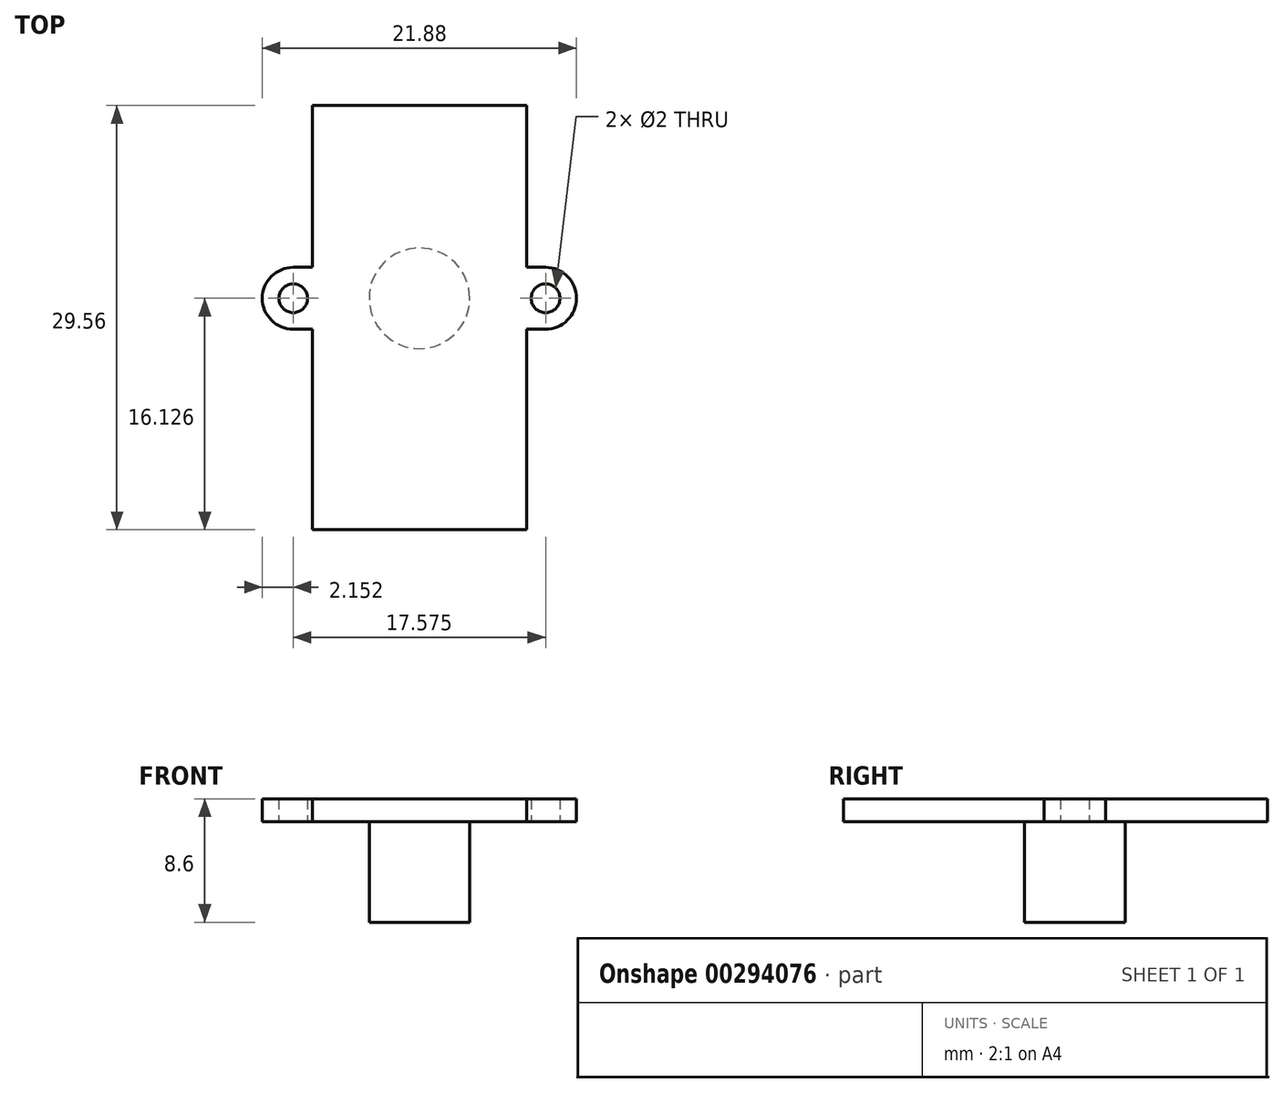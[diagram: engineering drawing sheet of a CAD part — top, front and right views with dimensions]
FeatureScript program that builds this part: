
annotation { "Feature Type Name" : "Feature", "Feature Type Description" : "" }
export const myFeature = defineFeature(function(context is Context, id is Id, definition is map)
    precondition{}
    {
        {
            var Q0;
            Q0=qCreatedBy(makeId("Top.planeOp"),FACE);
            var sketch = newSketch(context, id + "F0", { "sketchPlane" : qUnion([Q0])});
            skLineSegment(sketch, "E0.bottom", {"start": v(-23.3, 24.89) * mm, "end": v(-8.37, 24.89) * mm});
            skLineSegment(sketch, "E0.top", {"start": v(-23.3, -4.67) * mm, "end": v(-8.37, -4.67) * mm});
            skLineSegment(sketch, "E0.left", {"start": v(-23.3, 24.89) * mm, "end": v(-23.3, 13.61) * mm});
            skLineSegment(sketch, "E0.right", {"start": v(-8.37, 24.89) * mm, "end": v(-8.37, 13.61) * mm});
            skLineSegment(sketch, "E1", {"start": v(-23.3, 13.61) * mm, "end": v(-24.63, 13.61) * mm});
            skLineSegment(sketch, "E2", {"start": v(-23.3, 9.3) * mm, "end": v(-24.63, 9.3) * mm});
            skArc(sketch, "E3", {"start": v(-24.63, 13.61) * mm, "mid": v(-26.78, 11.46) * mm, "end": v(-24.63, 9.3) * mm});
            skLineSegment(sketch, "E4", {"start": v(-8.37, 13.61) * mm, "end": v(-7.05, 13.61) * mm});
            skLineSegment(sketch, "E5", {"start": v(-8.37, 9.3) * mm, "end": v(-7.05, 9.3) * mm});
            skArc(sketch, "E6", {"start": v(-7.05, 9.3) * mm, "mid": v(-4.9, 11.46) * mm, "end": v(-7.05, 13.61) * mm});
            skCircle(sketch, "E7", {"center": v(-24.63, 11.46) * mm, "radius": 1 * mm});
            skCircle(sketch, "E8", {"center": v(-7.05, 11.46) * mm, "radius": 1 * mm});
            skLineSegment(sketch, "E9.trimOffspring", {"start": v(-23.3, 9.3) * mm, "end": v(-23.3, -4.67) * mm});
            skLineSegment(sketch, "E10.trimOffspring", {"start": v(-8.37, 9.3) * mm, "end": v(-8.37, -4.67) * mm});
            skLineSegment(sketch, "E11", {"start": v(-24.63, 11.46) * mm, "end": v(-7.05, 11.46) * mm, "construction": true});
            skCircle(sketch, "E12", {"center": v(-15.84, 11.46) * mm, "radius": 3.5 * mm});
            skSolve(sketch);
        }
        {
            var Q0;
            Q0=makeQuery(id+"F0.imprint","IMPRINT",FACE,{"disambiguationData":[TD([[makeQuery(id+"F0.imprint","IMPRINT",EDGE,{"derivedFrom":sQuery(id+"F0.wireOp",EDGE,"E0.bottom")}),-1.0]])]});
            var Q1;
            Q1=makeQuery(id+"F0.imprint","IMPRINT",FACE,{"disambiguationData":[TD([[makeQuery(id+"F0.imprint","IMPRINT",EDGE,{"derivedFrom":sQuery(id+"F0.wireOp",EDGE,"E12")}),1.0]])]});
            extrude(context, id + "F1", {"entities" : qUnion([Q0, Q1]), "depth" : 1.6 * mm});
        }
        {
            var Q0;
            Q0=makeQuery(id+"F0.imprint","IMPRINT",FACE,{"disambiguationData":[TD([[makeQuery(id+"F0.imprint","IMPRINT",EDGE,{"derivedFrom":sQuery(id+"F0.wireOp",EDGE,"E12")}),1.0]])]});
            extrude(context, id + "F2", {"entities" : qUnion([Q0]), "operationType" : NewBodyOperationType.ADD, "oppositeDirection" : true, "depth" : 7 * mm});
        }
    });
